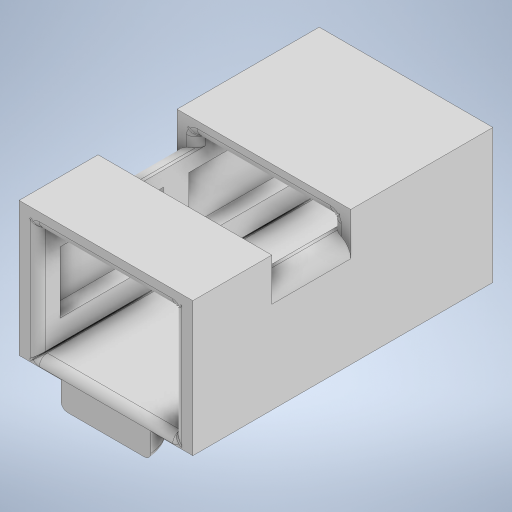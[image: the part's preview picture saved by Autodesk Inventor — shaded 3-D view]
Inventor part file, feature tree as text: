
AUTODESK INVENTOR PART (.ipt)
format: ipt  version: 2023 (Build 270158000, 158)  size: 682,496 bytes
history: native  units: in
note: dims shown in document units (in); Inventor stores cm internally (conversion verified against a paired STEP export)
features: projected_geometry x22, sketch x19, extrude x17, fillet x5
ambient origin geometry x8: Origin, YZ Plane, XZ Plane, XY Plane, X Axis, Y Axis, Z Axis, Center Point
bodies: Solid1 (feature_tree)
feature tree (63):
  extrude  "Extrusion1"  Depth=3.7402in
  extrude  "Extrusion2"  Depth=0.0984in
  extrude  "Extrusion3"  Depth=1.378in
  extrude  "Extrusion4"  Depth=1.7717in
  extrude  "Extrusion5"  Depth=0.2362in TaperAngle=0.0deg
  extrude  "Extrusion6"  Depth=0.9843in TaperAngle=0.0deg
  extrude  "Extrusion7"  Depth=0.0984in TaperAngle=0.0deg
  extrude  "Extrusion9"  Depth=0.0197in
  extrude  "Extrusion11"  Depth=0.0984in
  extrude  "Extrusion12"  Depth=0.6841in
  extrude  "Extrusion15"  TaperAngle=180.0deg  [1 undecoded]
  fillet  "Fillet1"  Radius=0.0197in
  fillet  "Fillet2"  Radius=0.0197in
  fillet  "Fillet3"  Radius=0.1181in
  fillet  "Fillet4"  Radius=0.0197in
  sketch  "Sketch17"  dims[d60=0.3937in d61=0.0in d66=0.3937in d67=0.0in d68=0.1969in]
  sketch  "Sketch18"  dims[d69=0.0984in d70=0.1181in]
  extrude  "Extrusion17"  Depth=0.3937in TaperAngle=0.0deg
  fillet  "Fillet5"  Radius=0.1969in
  extrude  "Extrusion18"  Depth=0.1181in
  extrude  "Extrusion19"  Depth=0.1181in
  extrude  "Extrusion20"  Depth=1.122in
  extrude  "Extrusion21"  Depth=0.0787in
  extrude  "Extrusion22"  Depth=0.6496in
  sketch  "Sketch1"  dims[d0=1.9685in d1=3.7402in]
  sketch  "Sketch2"  dims[d2=1.5748in d3=0.0in d4=0.0984in]
  projected_geometry  "Projected Loop1"
  sketch  "Sketch3"  dims[d5=1.7717in d6=1.378in]
  projected_geometry  "Projected Loop2"
  sketch  "Sketch4"  dims[d7=3.5433in d8=0.0in d9=1.7717in]
  projected_geometry  "Projected Loop3"
  sketch  "Sketch5"  dims[d10=2.7559in d11=0.2362in d12=0.0in]
  projected_geometry  "Projected Loop4"
  sketch  "Sketch6"  dims[d13=0.9843in d14=0.2362in d15=0.0in]
  projected_geometry  "Projected Loop5"
  sketch  "Sketch7"  dims[d16=0.0984in d17=0.0in d18=0.0984in d19=0.0in]
  projected_geometry  "Projected Loop6"
  projected_geometry  "Projected Loop7"
  sketch  "Sketch10"  dims[d20=0.0984in d21=0.0in d29=0.0197in]
  projected_geometry  "Projected Loop9"
  sketch  "Sketch11"  dims[d30=0.0984in d31=0.0in d49=0.8465in]
  projected_geometry  "Projected Loop10"
  sketch  "Sketch12"  dims[d50=0.8268in d51=0.6841in]
  projected_geometry  "Projected Loop11"
  sketch  "Sketch16"  dims[d52=0.3937in d53=0.0in d54=180.0deg d55=0.0197in d56=0.0197in d58=0.1181in d59=0.0197in]
  projected_geometry  "Projected Loop15"
  projected_geometry  "Projected Loop16"
  projected_geometry  "Projected Loop17"
  sketch  "Sketch20"  dims[d71=0.1181in d72=0.0394in]
  projected_geometry  "Projected Loop20"
  projected_geometry  "Projected Loop21"
  projected_geometry  "Projected Loop22"
  sketch  "Sketch21"  dims[d77=1.122in d78=1.122in]
  projected_geometry  "Projected Loop23"
  sketch  "Sketch22"  dims[d79=0.315in d80=0.0in d81=0.0787in]
  projected_geometry  "Projected Loop24"
  sketch  "Sketch23"  dims[d83=0.7677in d84=0.6496in]
  projected_geometry  "Projected Loop25"
  projected_geometry  "Projected Loop26"
  sketch  "Sketch24"  dims[d85=0.1969in]
  projected_geometry  "Projected Loop27"
  sketch  "Sketch25"  dims[d86=0.3543in d87=0.0in d88=1.2894in d89=0.7677in d90=0.2677in d91=0.3074in d92=0.1575in d93=1.2894in d94=0.7677in d95=0.315in d96=0.187in d97=0.0in d98=0.187in d99=0.0in d100=0.7677in d101=1.2894in d102=0.0394in d103=0.7677in d104=1.2894in d105=0.0472in d106=0.0395in d107=0.1575in d108=0.0in d109=0.7677in d110=0.6496in d111=0.7677in d112=0.6496in d113=0.0469in d114=0.0394in d115=0.0399in d116=0.1575in d117=0.0in]
  projected_geometry  "Projected Loop28"
note: 1 required parameter value undecoded (feature->parameter linkage not recoverable at this tier; creation-order binding heuristic only, values carry confidence <= 0.55)
